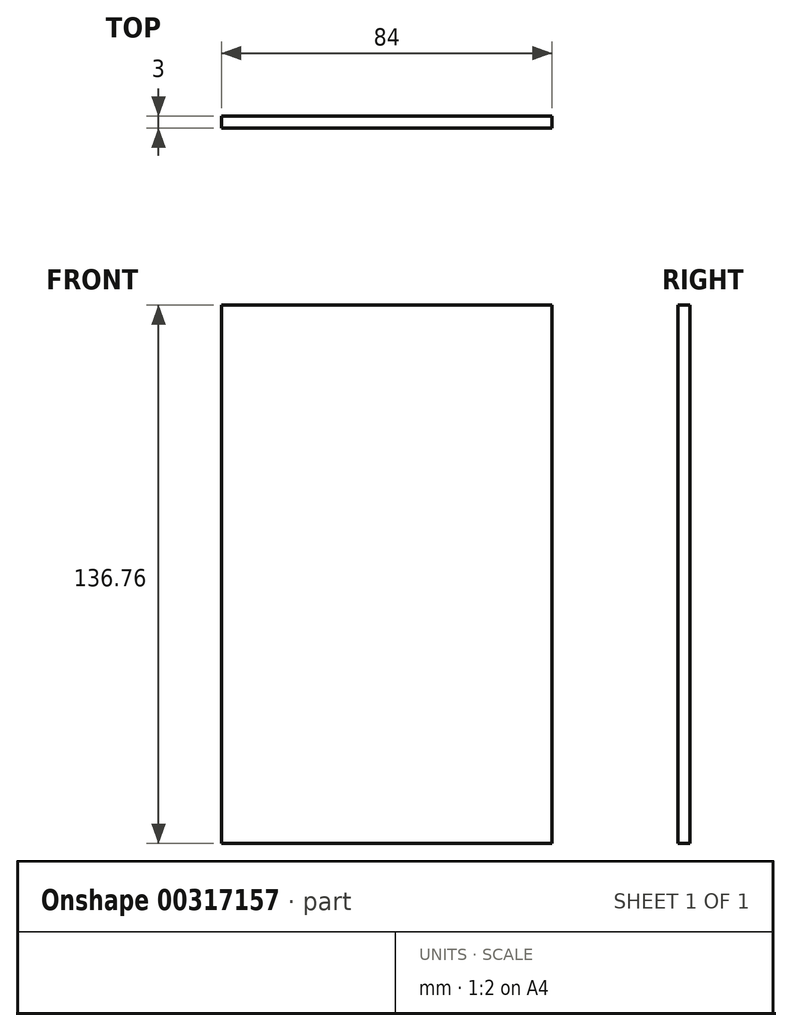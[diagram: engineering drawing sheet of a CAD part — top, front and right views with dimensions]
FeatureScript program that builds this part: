
annotation { "Feature Type Name" : "Feature", "Feature Type Description" : "" }
export const myFeature = defineFeature(function(context is Context, id is Id, definition is map)
    precondition{}
    {
        {
            var Q0;
            Q0=qCreatedBy(makeId("Front.planeOp"),FACE);
            var sketch = newSketch(context, id + "F0", { "sketchPlane" : qUnion([Q0])});
            skLineSegment(sketch, "E0.bottom", {"start": v(42, 68.38) * mm, "end": v(-42, 68.38) * mm});
            skLineSegment(sketch, "E0.top", {"start": v(42, -68.37) * mm, "end": v(-42, -68.37) * mm});
            skLineSegment(sketch, "E0.left", {"start": v(42, 68.38) * mm, "end": v(42, -68.37) * mm});
            skLineSegment(sketch, "E0.right", {"start": v(-42, 68.38) * mm, "end": v(-42, -68.37) * mm});
            skPoint(sketch, "E0.middle", {"position": v(0, 0) * mm});
            skSolve(sketch);
        }
        {
            var Q0;
            Q0 = qSketchRegion(id + "F0", true);
            extrude(context, id + "F1", {"entities" : qUnion([Q0]), "depth" : 3 * mm});
        }
    });
